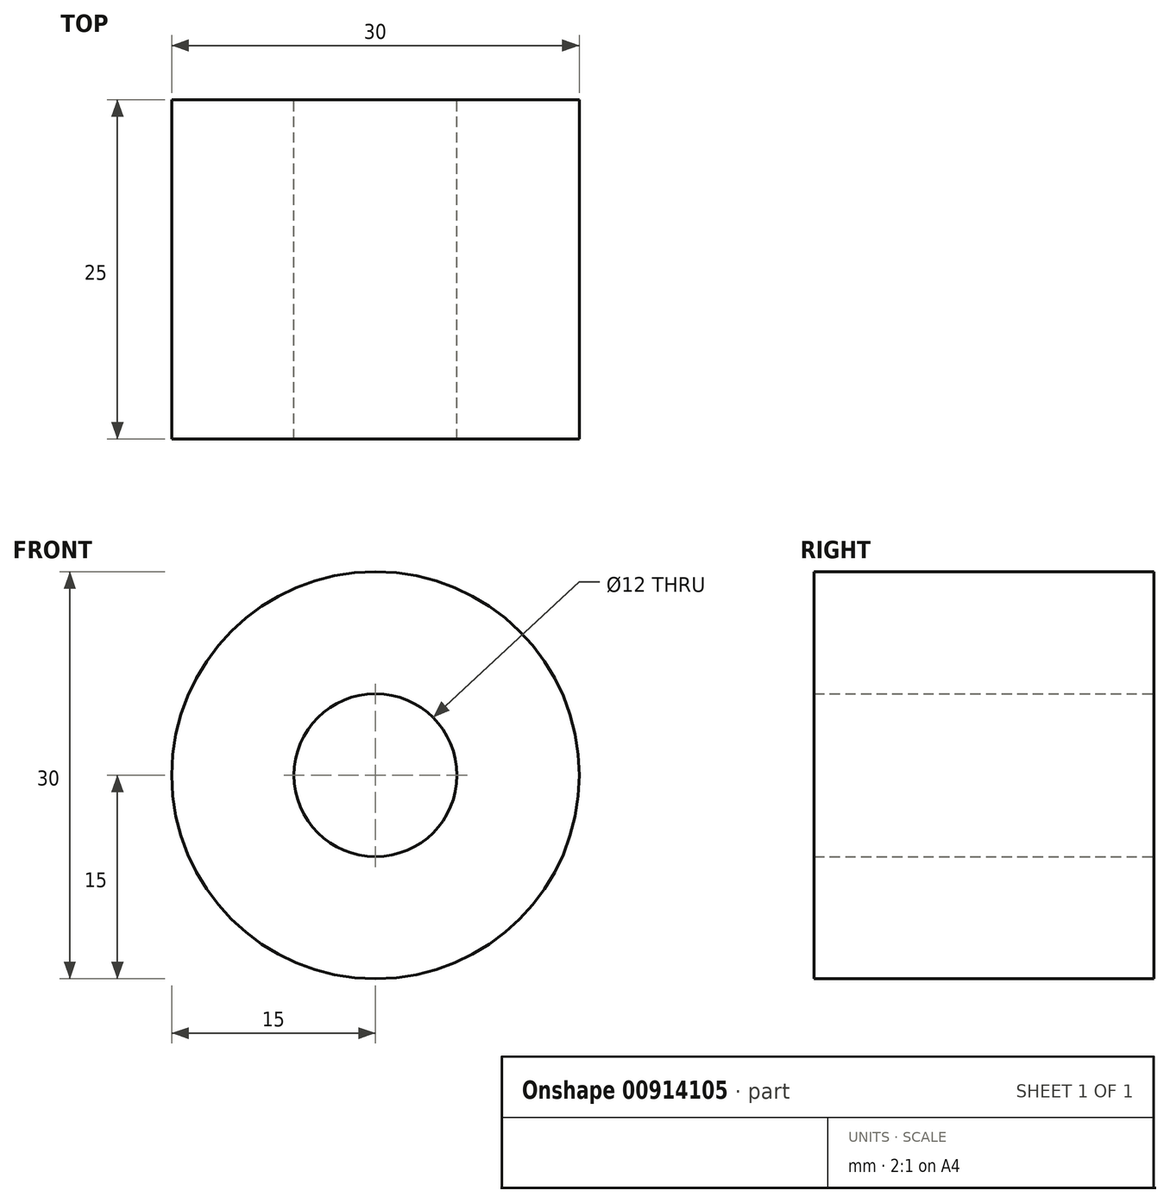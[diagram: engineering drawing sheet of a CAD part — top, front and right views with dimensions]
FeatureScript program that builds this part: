
annotation { "Feature Type Name" : "Feature", "Feature Type Description" : "" }
export const myFeature = defineFeature(function(context is Context, id is Id, definition is map)
    precondition{}
    {
        {
            var Q0;
            Q0=qCreatedBy(makeId("Front.planeOp"),FACE);
            var sketch = newSketch(context, id + "F0", { "sketchPlane" : qUnion([Q0])});
            skCircle(sketch, "E0", {"center": v(0, 0) * mm, "radius": 15 * mm});
            skCircle(sketch, "E1", {"center": v(0, 0) * mm, "radius": 6 * mm});
            skSolve(sketch);
        }
        {
            var Q0;
            Q0=makeQuery(id+"F0.imprint","IMPRINT",FACE,{"disambiguationData":[TD([[makeQuery(id+"F0.imprint","IMPRINT",EDGE,{"derivedFrom":sQuery(id+"F0.wireOp",EDGE,"E0")}),1.0]])]});
            extrude(context, id + "F1", {"entities" : qUnion([Q0]), "depth" : 25 * mm, "offsetDistance" : 25 * mm});
        }
    });
